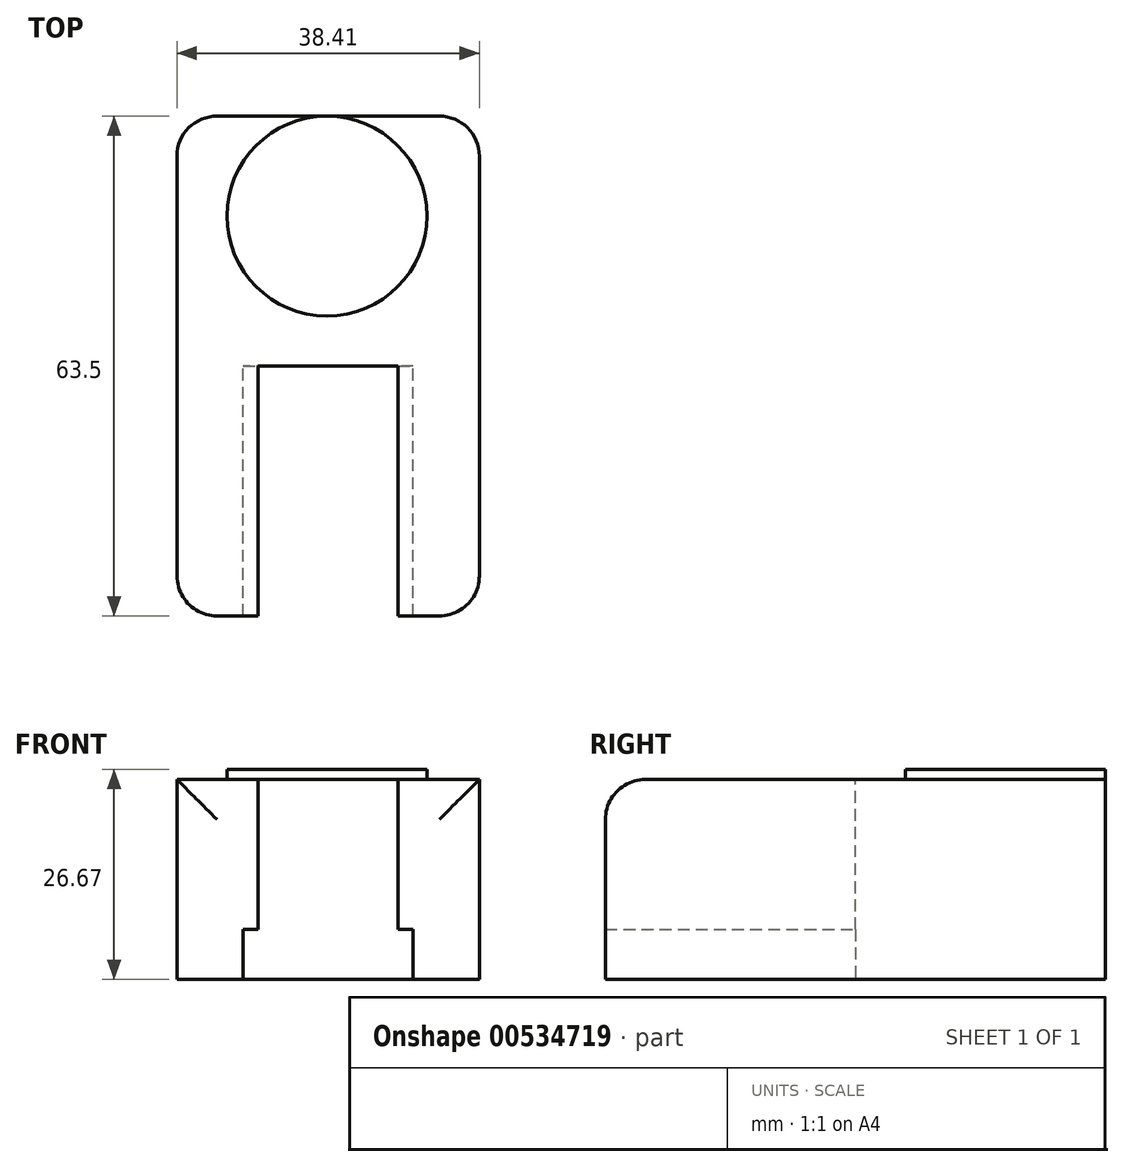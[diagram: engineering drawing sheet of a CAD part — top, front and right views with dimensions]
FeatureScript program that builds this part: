
annotation { "Feature Type Name" : "Feature", "Feature Type Description" : "" }
export const myFeature = defineFeature(function(context is Context, id is Id, definition is map)
    precondition{}
    {
        {
            var Q0;
            Q0=qCreatedBy(makeId("Top.planeOp"),FACE);
            var sketch = newSketch(context, id + "F0", { "sketchPlane" : qUnion([Q0])});
            skCircle(sketch, "E0", {"center": v(0, 0) * mm, "radius": 12.7 * mm});
            skSolve(sketch);
        }
        {
            var Q0;
            Q0=makeQuery(id+"F0.imprint","IMPRINT",FACE,{"disambiguationData":[TD([[makeQuery(id+"F0.imprint","IMPRINT",EDGE,{"derivedFrom":sQuery(id+"F0.wireOp",EDGE,"E0")}),1.0]])]});
            extrude(context, id + "F1", {"entities" : qUnion([Q0]), "depth" : 1.27 * mm, "offsetDistance" : 25.4 * mm});
        }
        {
            var Q0;
            Q0=qCreatedBy(makeId("Top.planeOp"),FACE);
            var sketch = newSketch(context, id + "F2", { "sketchPlane" : qUnion([Q0])});
            skLineSegment(sketch, "E1.bottom", {"start": v(-19.05, 12.7) * mm, "end": v(19.36, 12.7) * mm});
            skLineSegment(sketch, "E1.left", {"start": v(-19.05, 12.7) * mm, "end": v(-19.05, -50.8) * mm});
            skLineSegment(sketch, "E1.right", {"start": v(19.36, 12.7) * mm, "end": v(19.36, -50.8) * mm});
            skLineSegment(sketch, "E2", {"start": v(19.36, -50.8) * mm, "end": v(9.04, -50.8) * mm});
            skLineSegment(sketch, "E3", {"start": v(9.04, -50.8) * mm, "end": v(9.04, -19.05) * mm});
            skLineSegment(sketch, "E4", {"start": v(9.04, -19.05) * mm, "end": v(-8.74, -19.05) * mm});
            skLineSegment(sketch, "E5", {"start": v(-19.05, -50.8) * mm, "end": v(-8.74, -50.8) * mm});
            skLineSegment(sketch, "E6", {"start": v(-8.74, -50.8) * mm, "end": v(-8.74, -19.05) * mm});
            skSolve(sketch);
        }
        {
            var Q0;
            Q0=makeQuery(id+"F2.imprint","IMPRINT",FACE,{"disambiguationData":[TD([[makeQuery(id+"F2.imprint","IMPRINT",EDGE,{"derivedFrom":sQuery(id+"F2.wireOp",EDGE,"E1.bottom")}),-1.0]])]});
            extrude(context, id + "F3", {"entities" : qUnion([Q0]), "operationType" : NewBodyOperationType.ADD, "oppositeDirection" : true, "depth" : 25.4 * mm, "offsetDistance" : 25.4 * mm});
        }
        {
            var Q0;
            Q0=makeQuery(id+"F3.opExtrude","CAP_FACE",FACE,{"disambiguationData":[OSD([sQuery(id+"F2.wireOp",EDGE,"E1.bottom"),sQuery(id+"F2.wireOp",EDGE,"E1.left"),sQuery(id+"F2.wireOp",EDGE,"E1.right"),sQuery(id+"F2.wireOp",EDGE,"E2"),sQuery(id+"F2.wireOp",EDGE,"E3"),sQuery(id+"F2.wireOp",EDGE,"E4"),sQuery(id+"F2.wireOp",EDGE,"E5"),sQuery(id+"F2.wireOp",EDGE,"E6")])],"isStart":true});
            var sketch = newSketch(context, id + "F4", { "sketchPlane" : qUnion([Q0])});
            skSolve(sketch);
        }
        {
            var Q0;
            Q0=makeQuery(id+"F3.opExtrude","CAP_FACE",FACE,{"disambiguationData":[OSD([sQuery(id+"F2.wireOp",EDGE,"E1.bottom"),sQuery(id+"F2.wireOp",EDGE,"E1.left"),sQuery(id+"F2.wireOp",EDGE,"E1.right"),sQuery(id+"F2.wireOp",EDGE,"E2"),sQuery(id+"F2.wireOp",EDGE,"E3"),sQuery(id+"F2.wireOp",EDGE,"E4"),sQuery(id+"F2.wireOp",EDGE,"E5"),sQuery(id+"F2.wireOp",EDGE,"E6")])],"isStart":false});
            var sketch = newSketch(context, id + "F5", { "sketchPlane" : qUnion([Q0])});
            skLineSegment(sketch, "E7.bottom", {"start": v(-10.64, 50.8) * mm, "end": v(10.95, 50.8) * mm});
            skLineSegment(sketch, "E7.top", {"start": v(-10.64, 19.05) * mm, "end": v(10.95, 19.05) * mm});
            skLineSegment(sketch, "E7.left", {"start": v(-10.64, 50.8) * mm, "end": v(-10.64, 19.05) * mm});
            skLineSegment(sketch, "E7.right", {"start": v(10.95, 50.8) * mm, "end": v(10.95, 19.05) * mm});
            skSolve(sketch);
        }
        {
            var Q0;
            {var subQ2=sQuery(id+"F5.wireOp",EDGE,"E7.left");Q0=makeQuery(id+"F5.imprint","IMPRINT",FACE,{"disambiguationData":[TD([[makeQuery(id+"F5.imprint","IMPRINT",EDGE,{"derivedFrom":subQ2}),1.0]])]});}
            var Q1;
            {var subQ2=sQuery(id+"F5.wireOp",EDGE,"E7.right");Q1=makeQuery(id+"F5.imprint","IMPRINT",FACE,{"disambiguationData":[TD([[makeQuery(id+"F5.imprint","IMPRINT",EDGE,{"derivedFrom":subQ2}),-1.0]])]});}
            extrude(context, id + "F6", {"entities" : qUnion([Q0, Q1]), "operationType" : NewBodyOperationType.REMOVE, "oppositeDirection" : true, "depth" : 6.35 * mm, "offsetDistance" : 25.4 * mm});
        }
        {
            var Q0;
            Q0=makeQuery(id+"F3.opExtrude","CAP_EDGE",EDGE,{"disambiguationData":[OSD([sQuery(id+"F2.wireOp",EDGE,"E5")])],"isStart":true});
            var Q1;
            Q1=makeQuery(id+"F3.opExtrude","SWEPT_EDGE",EDGE,{"disambiguationData":[OSD([sQuery(id+"F2.wireOp",EDGE,"E1.left"),sQuery(id+"F2.wireOp",EDGE,"E5")])]});
            var Q2;
            Q2=makeQuery(id+"F3.opExtrude","CAP_EDGE",EDGE,{"disambiguationData":[OSD([sQuery(id+"F2.wireOp",EDGE,"E2")])],"isStart":true});
            var Q3;
            Q3=makeQuery(id+"F3.opExtrude","SWEPT_EDGE",EDGE,{"disambiguationData":[OSD([sQuery(id+"F2.wireOp",EDGE,"E1.right"),sQuery(id+"F2.wireOp",EDGE,"E2")])]});
            var Q4;
            Q4=makeQuery(id+"F3.opExtrude","SWEPT_EDGE",EDGE,{"disambiguationData":[OSD([sQuery(id+"F2.wireOp",EDGE,"E1.bottom"),sQuery(id+"F2.wireOp",EDGE,"E1.right")])]});
            var Q5;
            Q5=makeQuery(id+"F3.opExtrude","SWEPT_EDGE",EDGE,{"disambiguationData":[OSD([sQuery(id+"F2.wireOp",EDGE,"E1.bottom"),sQuery(id+"F2.wireOp",EDGE,"E1.left")])]});
            fillet(context, id + "F7", {"entities" : qUnion([Q0, Q1, Q2, Q3, Q4, Q5]), "radius" : 5.08 * mm, "tangentPropagation" : true, "allowEdgeOverflow" : false});
        }
    });
